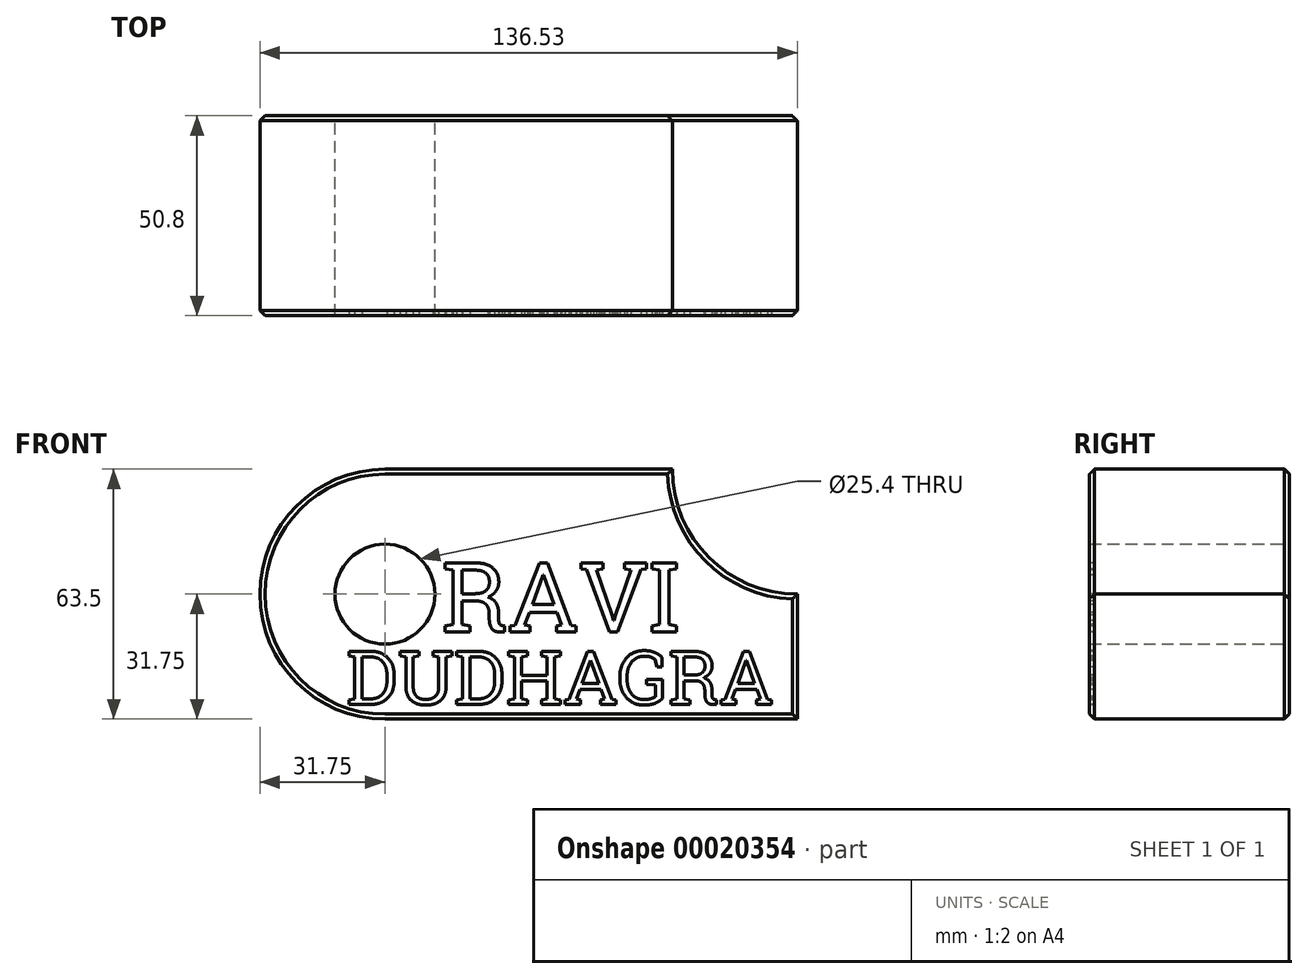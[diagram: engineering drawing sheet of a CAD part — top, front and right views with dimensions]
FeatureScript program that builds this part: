
annotation { "Feature Type Name" : "Feature", "Feature Type Description" : "" }
export const myFeature = defineFeature(function(context is Context, id is Id, definition is map)
    precondition{}
    {
        {
            var Q0;
            Q0=qCreatedBy(makeId("Front.planeOp"),FACE);
            var sketch = newSketch(context, id + "F0", { "sketchPlane" : qUnion([Q0])});
            skLineSegment(sketch, "E0", {"start": v(0, 0) * mm, "end": v(104.77, 0) * mm});
            skLineSegment(sketch, "E1", {"start": v(104.78, 0) * mm, "end": v(104.78, 31.75) * mm});
            skArc(sketch, "E2", {"start": v(73.03, 63.5) * mm, "mid": v(82.32, 41.05) * mm, "end": v(104.78, 31.75) * mm});
            skLineSegment(sketch, "E3", {"start": v(0, 63.5) * mm, "end": v(73.03, 63.5) * mm});
            skArc(sketch, "E4", {"start": v(0, 63.5) * mm, "mid": v(-31.75, 31.75) * mm, "end": v(0, 0) * mm});
            skCircle(sketch, "E5", {"center": v(0, 31.75) * mm, "radius": 12.7 * mm});
            skSolve(sketch);
        }
        {
            var Q0;
            Q0=makeQuery(id+"F0.imprint","IMPRINT",FACE,{"disambiguationData":[TD([[makeQuery(id+"F0.imprint","IMPRINT",EDGE,{"derivedFrom":sQuery(id+"F0.wireOp",EDGE,"E0")}),1.0]])]});
            extrude(context, id + "F1", {"entities" : qUnion([Q0]), "depth" : 50.8 * mm});
        }
        {
            var Q0;
            Q0=makeQuery(id+"F1.opExtrude","CAP_FACE",FACE,{"disambiguationData":[OSD([sQuery(id+"F0.wireOp",EDGE,"E0"),sQuery(id+"F0.wireOp",EDGE,"E1"),sQuery(id+"F0.wireOp",EDGE,"E2"),sQuery(id+"F0.wireOp",EDGE,"E3"),sQuery(id+"F0.wireOp",EDGE,"E4"),sQuery(id+"F0.wireOp",EDGE,"E5")])],"isStart":false});
            var sketch = newSketch(context, id + "F2", { "sketchPlane" : qUnion([Q0])});
            skText(sketch, "E6", { "text": "RAVI", "fontName": "RobotoSlab-Regular.ttf"});
            skText(sketch, "E7", { "text": "DUDHAGRA", "fontName": "RobotoSlab-Regular.ttf"});
            const initialGuessF2  = {"E6": [0.01444, 0.02216, 1, 0, 0.01778], "E7": [-0.00983, 0.00375, 1, 0, 0.01365]};
            skSetInitialGuess(sketch, initialGuessF2);
            skSolve(sketch);
        }
        {
            var Q0;
            Q0 = qSketchRegion(id + "F2", true);
            extrude(context, id + "F3", {"entities" : qUnion([Q0]), "operationType" : NewBodyOperationType.REMOVE, "oppositeDirection" : true, "depth" : 1.27 * mm});
        }
        {
            var Q0;
            Q0=makeQuery(id+"F1.opExtrude","CAP_EDGE",EDGE,{"disambiguationData":[OSD([sQuery(id+"F0.wireOp",EDGE,"E2")])],"isStart":true});
            var Q1;
            Q1=makeQuery(id+"F1.opExtrude","CAP_EDGE",EDGE,{"disambiguationData":[OSD([sQuery(id+"F0.wireOp",EDGE,"E1")])],"isStart":true});
            var Q2;
            Q2=makeQuery(id+"F1.opExtrude","CAP_EDGE",EDGE,{"disambiguationData":[OSD([sQuery(id+"F0.wireOp",EDGE,"E3")])],"isStart":true});
            var Q3;
            Q3=makeQuery(id+"F1.opExtrude","CAP_EDGE",EDGE,{"disambiguationData":[OSD([sQuery(id+"F0.wireOp",EDGE,"E4")])],"isStart":false});
            var Q4;
            Q4=makeQuery(id+"F1.opExtrude","CAP_EDGE",EDGE,{"disambiguationData":[OSD([sQuery(id+"F0.wireOp",EDGE,"E0")])],"isStart":false});
            var Q5;
            Q5=makeQuery(id+"F1.opExtrude","CAP_EDGE",EDGE,{"disambiguationData":[OSD([sQuery(id+"F0.wireOp",EDGE,"E1")])],"isStart":false});
            var Q6;
            Q6=makeQuery(id+"F1.opExtrude","CAP_EDGE",EDGE,{"disambiguationData":[OSD([sQuery(id+"F0.wireOp",EDGE,"E2")])],"isStart":false});
            var Q7;
            Q7=makeQuery(id+"F1.opExtrude","CAP_EDGE",EDGE,{"disambiguationData":[OSD([sQuery(id+"F0.wireOp",EDGE,"E3")])],"isStart":false});
            chamfer(context, id + "F4", {"entities" : qUnion([Q0, Q1, Q2, Q3, Q4, Q5, Q6, Q7]), "width" : 1.27 * mm, "tangentPropagation" : true});
        }
    });
